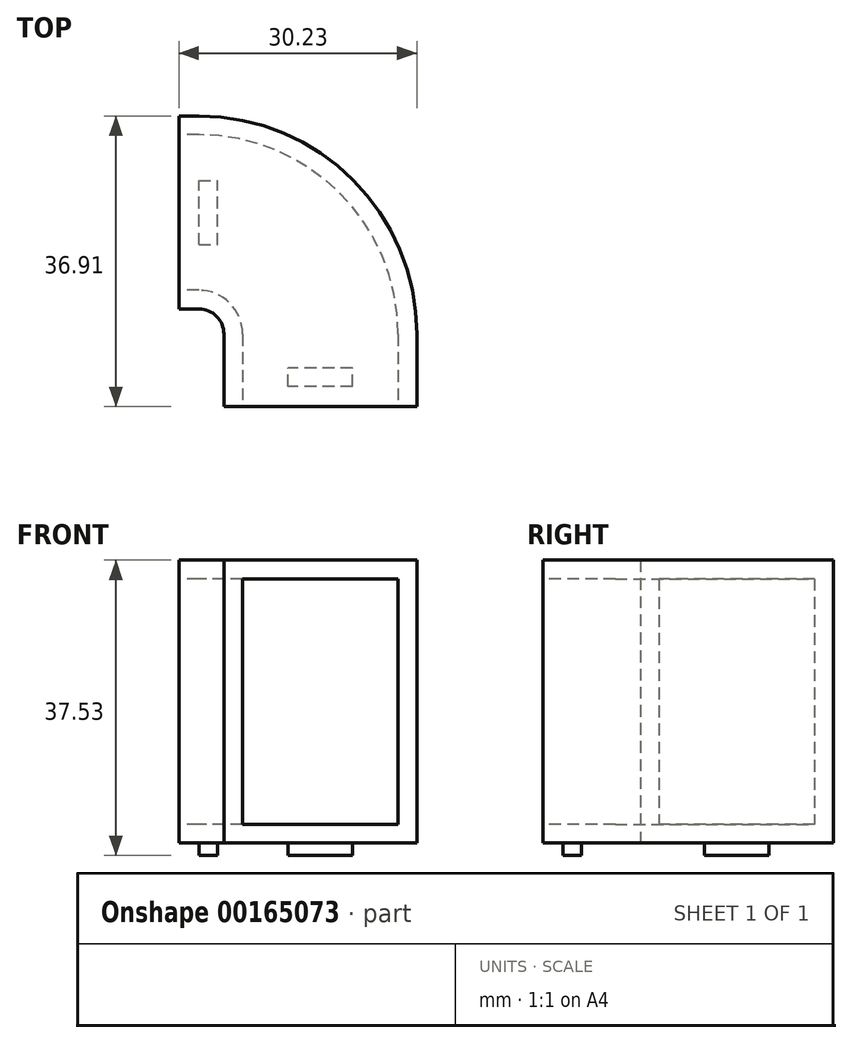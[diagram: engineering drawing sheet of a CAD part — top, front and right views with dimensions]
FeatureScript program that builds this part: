
annotation { "Feature Type Name" : "Feature", "Feature Type Description" : "" }
export const myFeature = defineFeature(function(context is Context, id is Id, definition is map)
    precondition{}
    {
        {
            var Q0;
            Q0=qCreatedBy(makeId("Top.planeOp"),FACE);
            var sketch = newSketch(context, id + "F0", { "sketchPlane" : qUnion([Q0])});
            skLineSegment(sketch, "E0.bottom", {"start": v(0, 0) * mm, "end": v(-2.54, 0) * mm});
            skLineSegment(sketch, "E0.top", {"start": v(0, -24.52) * mm, "end": v(-2.54, -24.52) * mm});
            skLineSegment(sketch, "E0.left", {"start": v(0, 0) * mm, "end": v(0, -24.52) * mm, "construction": true});
            skLineSegment(sketch, "E0.right", {"start": v(-2.54, 0) * mm, "end": v(-2.54, -24.52) * mm});
            skArc(sketch, "E1", {"start": v(3.18, -27.7) * mm, "mid": v(2.25, -25.45) * mm, "end": v(0, -24.52) * mm});
            skArc(sketch, "E2", {"start": v(27.7, -27.7) * mm, "mid": v(19.58, -8.11) * mm, "end": v(0, 0) * mm});
            skLineSegment(sketch, "E3.bottom", {"start": v(3.18, -27.7) * mm, "end": v(27.7, -27.7) * mm, "construction": true});
            skLineSegment(sketch, "E3.top", {"start": v(3.18, -36.9) * mm, "end": v(27.7, -36.9) * mm});
            skLineSegment(sketch, "E3.left", {"start": v(3.18, -27.7) * mm, "end": v(3.18, -36.9) * mm});
            skLineSegment(sketch, "E3.right", {"start": v(27.7, -27.7) * mm, "end": v(27.7, -36.9) * mm});
            skSolve(sketch);
        }
        {
            var Q0;
            Q0=qSketchRegion(id+"F0",true);
            extrude(context, id + "F1", {"entities" : qUnion([Q0]), "depth" : 35.94 * mm});
        }
        {
            var Q0;
            Q0=makeQuery(id+"F1.opExtrude","SWEPT_FACE",FACE,{"disambiguationData":[OSD([sQuery(id+"F0.wireOp",EDGE,"E0.right")])]});
            shell(context, id + "F2", {"entities" : qUnion([Q0]), "thickness" : 2.38 * mm});
        }
        {
            var Q0;
            Q0=makeQuery(id+"F1.opExtrude","SWEPT_FACE",FACE,{"disambiguationData":[OSD([sQuery(id+"F0.wireOp",EDGE,"E3.top")])]});
            var sketch = newSketch(context, id + "F3", { "sketchPlane" : qUnion([Q0])});
            skLineSegment(sketch, "E4.bottom", {"start": v(3.18, 35.94) * mm, "end": v(5.56, 35.94) * mm, "construction": true});
            skLineSegment(sketch, "E4.top", {"start": v(3.18, 33.56) * mm, "end": v(5.56, 33.56) * mm, "construction": true});
            skLineSegment(sketch, "E4.left", {"start": v(3.18, 35.94) * mm, "end": v(3.18, 33.56) * mm, "construction": true});
            skLineSegment(sketch, "E4.right", {"start": v(5.56, 35.94) * mm, "end": v(5.56, 33.56) * mm, "construction": true});
            skLineSegment(sketch, "E5.bottom", {"start": v(27.7, 0) * mm, "end": v(25.31, 0) * mm, "construction": true});
            skLineSegment(sketch, "E5.top", {"start": v(27.7, 2.38) * mm, "end": v(25.31, 2.38) * mm, "construction": true});
            skLineSegment(sketch, "E5.left", {"start": v(27.7, 0) * mm, "end": v(27.7, 2.38) * mm, "construction": true});
            skLineSegment(sketch, "E5.right", {"start": v(25.31, 0) * mm, "end": v(25.31, 2.38) * mm, "construction": true});
            skLineSegment(sketch, "E6.bottom", {"start": v(5.56, 33.56) * mm, "end": v(25.31, 33.56) * mm});
            skLineSegment(sketch, "E6.top", {"start": v(5.56, 2.38) * mm, "end": v(25.31, 2.38) * mm});
            skLineSegment(sketch, "E6.left", {"start": v(5.56, 33.56) * mm, "end": v(5.56, 2.38) * mm});
            skLineSegment(sketch, "E6.right", {"start": v(25.31, 33.56) * mm, "end": v(25.31, 2.38) * mm});
            skSolve(sketch);
        }
        {
            var Q0;
            Q0=qSketchRegion(id+"F3",true);
            extrude(context, id + "F4", {"entities" : qUnion([Q0]), "operationType" : NewBodyOperationType.REMOVE, "oppositeDirection" : true, "depth" : 2.38 * mm});
        }
        {
            var Q0;
            Q0=makeQuery(id+"F1.opExtrude","CAP_FACE",FACE,{"disambiguationData":[OSD([sQuery(id+"F0.wireOp",EDGE,"E0.bottom"),sQuery(id+"F0.wireOp",EDGE,"E0.top"),sQuery(id+"F0.wireOp",EDGE,"E0.right"),sQuery(id+"F0.wireOp",EDGE,"E1"),sQuery(id+"F0.wireOp",EDGE,"E2"),sQuery(id+"F0.wireOp",EDGE,"E3.top"),sQuery(id+"F0.wireOp",EDGE,"E3.left"),sQuery(id+"F0.wireOp",EDGE,"E3.right")])],"isStart":true});
            var sketch = newSketch(context, id + "F5", { "sketchPlane" : qUnion([Q0])});
            skLineSegment(sketch, "E7.bottom", {"start": v(0, 8.17) * mm, "end": v(2.38, 8.17) * mm});
            skLineSegment(sketch, "E7.top", {"start": v(0, 16.35) * mm, "end": v(2.38, 16.35) * mm});
            skLineSegment(sketch, "E7.left", {"start": v(0, 16.35) * mm, "end": v(0, 8.17) * mm});
            skLineSegment(sketch, "E7.right", {"start": v(2.38, 16.35) * mm, "end": v(2.38, 8.17) * mm});
            skLineSegment(sketch, "E8", {"start": v(0, 8.17) * mm, "end": v(0, 0) * mm, "construction": true});
            skLineSegment(sketch, "E9", {"start": v(0, 16.35) * mm, "end": v(0, 24.52) * mm, "construction": true});
            skLineSegment(sketch, "E10.bottom", {"start": v(19.52, 34.37) * mm, "end": v(11.35, 34.37) * mm});
            skLineSegment(sketch, "E10.top", {"start": v(19.52, 31.99) * mm, "end": v(11.35, 31.99) * mm});
            skLineSegment(sketch, "E10.left", {"start": v(19.52, 34.37) * mm, "end": v(19.52, 31.99) * mm});
            skLineSegment(sketch, "E10.right", {"start": v(11.35, 34.37) * mm, "end": v(11.35, 31.99) * mm});
            skLineSegment(sketch, "E11", {"start": v(15.43, 34.37) * mm, "end": v(15.43, 36.9) * mm, "construction": true});
            skPoint(sketch, "E12", {"position": v(2.38, 12.26) * mm});
            skSolve(sketch);
        }
        {
            var Q0;
            Q0=qSketchRegion(id+"F5",true);
            extrude(context, id + "F6", {"entities" : qUnion([Q0]), "operationType" : NewBodyOperationType.ADD, "depth" : 1.59 * mm});
        }
    });
